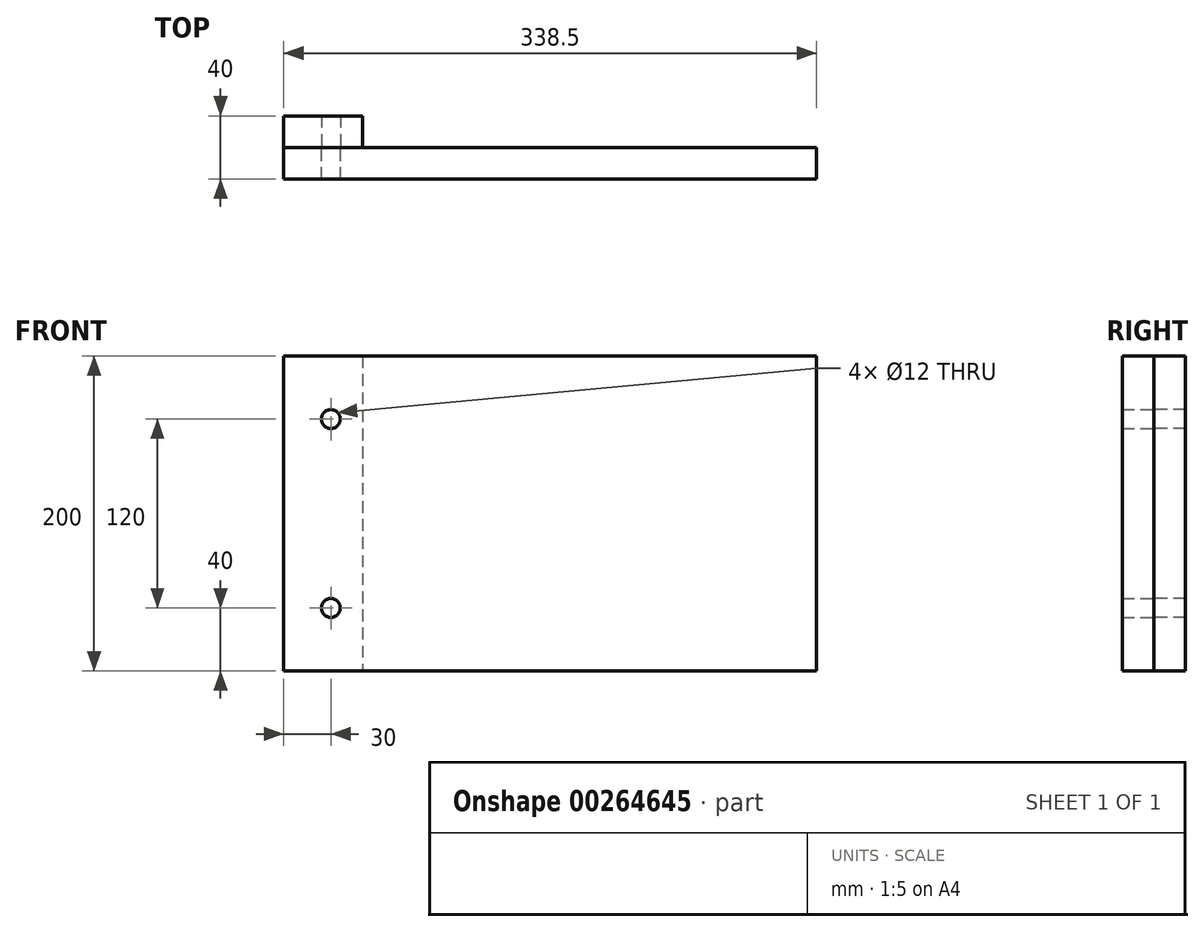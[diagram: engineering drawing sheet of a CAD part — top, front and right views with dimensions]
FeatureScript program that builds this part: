
annotation { "Feature Type Name" : "Feature", "Feature Type Description" : "" }
export const myFeature = defineFeature(function(context is Context, id is Id, definition is map)
    precondition{}
    {
        {
            var Q0;
            Q0=qCreatedBy(makeId("Front.planeOp"),FACE);
            var sketch = newSketch(context, id + "F0", { "sketchPlane" : qUnion([Q0])});
            skLineSegment(sketch, "E0.bottom", {"start": v(0, 0) * mm, "end": v(338.5, 0) * mm});
            skLineSegment(sketch, "E0.top", {"start": v(0, 200) * mm, "end": v(338.5, 200) * mm});
            skLineSegment(sketch, "E0.left", {"start": v(0, 0) * mm, "end": v(0, 200) * mm});
            skLineSegment(sketch, "E0.right", {"start": v(338.5, 0) * mm, "end": v(338.5, 200) * mm});
            skLineSegment(sketch, "E1", {"start": v(50, 200) * mm, "end": v(50, 0) * mm});
            skLineSegment(sketch, "E2", {"start": v(30, 200) * mm, "end": v(30, 0) * mm, "construction": true});
            skCircle(sketch, "E3", {"center": v(30, 160) * mm, "radius": 6 * mm});
            skCircle(sketch, "E4", {"center": v(30, 40) * mm, "radius": 6 * mm});
            skSolve(sketch);
        }
        {
            var Q0;
            {var subQ0=sQuery(id+"F0.wireOp",EDGE,"E0.right");Q0=makeQuery(id+"F0.imprint","IMPRINT",FACE,{"disambiguationData":[TD([[makeQuery(id+"F0.imprint","IMPRINT",EDGE,{"derivedFrom":subQ0}),1.0]])]});}
            var Q1;
            {var subQ1=sQuery(id+"F0.wireOp",EDGE,"E0.left");Q1=makeQuery(id+"F0.imprint","IMPRINT",FACE,{"disambiguationData":[TD([[makeQuery(id+"F0.imprint","IMPRINT",EDGE,{"derivedFrom":subQ1}),-1.0]])]});}
            extrude(context, id + "F1", {"entities" : qUnion([Q0, Q1]), "depth" : 20 * mm});
        }
        {
            var Q0;
            {var subQ1=sQuery(id+"F0.wireOp",EDGE,"E0.left");Q0=makeQuery(id+"F0.imprint","IMPRINT",FACE,{"disambiguationData":[TD([[makeQuery(id+"F0.imprint","IMPRINT",EDGE,{"derivedFrom":subQ1}),-1.0]])]});}
            extrude(context, id + "F2", {"entities" : qUnion([Q0]), "oppositeDirection" : true, "depth" : 20 * mm});
        }
    });
